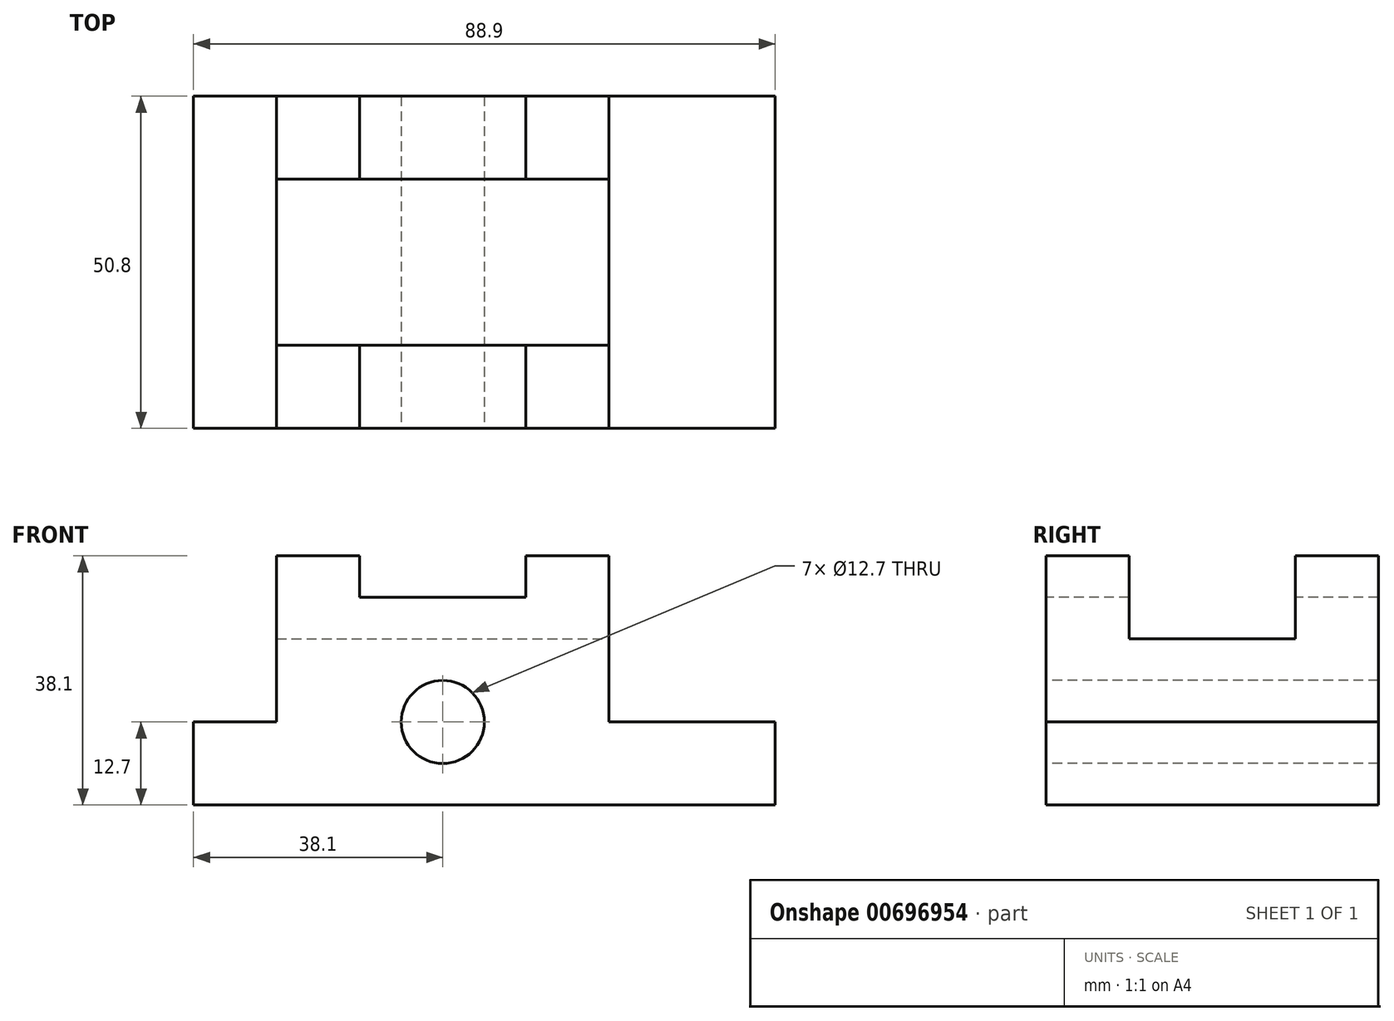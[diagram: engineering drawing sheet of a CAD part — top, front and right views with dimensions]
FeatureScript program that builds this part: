
annotation { "Feature Type Name" : "Feature", "Feature Type Description" : "" }
export const myFeature = defineFeature(function(context is Context, id is Id, definition is map)
    precondition{}
    {
        {
            var Q0;
            Q0=qCreatedBy(makeId("Front.planeOp"),FACE);
            var sketch = newSketch(context, id + "F0", { "sketchPlane" : qUnion([Q0])});
            skLineSegment(sketch, "E0.bottom", {"start": v(-44.45, 19.05) * mm, "end": v(44.45, 19.05) * mm});
            skLineSegment(sketch, "E0.top", {"start": v(-44.45, -19.05) * mm, "end": v(44.45, -19.05) * mm});
            skLineSegment(sketch, "E0.left", {"start": v(-44.45, 19.05) * mm, "end": v(-44.45, -19.05) * mm});
            skLineSegment(sketch, "E0.right", {"start": v(44.45, 19.05) * mm, "end": v(44.45, -19.05) * mm});
            skPoint(sketch, "E0.middle", {"position": v(0, 0) * mm});
            skSolve(sketch);
        }
        {
            var Q0;
            Q0=makeQuery(id+"F0.imprint","IMPRINT",FACE,{"disambiguationData":[TD([[makeQuery(id+"F0.imprint","IMPRINT",EDGE,{"derivedFrom":sQuery(id+"F0.wireOp",EDGE,"E0.bottom")}),-1.0]])]});
            extrude(context, id + "F1", {"entities" : qUnion([Q0]), "depth" : 50.8 * mm, "offsetDistance" : 25.4 * mm});
        }
        {
            var Q0;
            Q0=makeQuery(id+"F1.opExtrude","CAP_FACE",FACE,{"disambiguationData":[OSD([sQuery(id+"F0.wireOp",EDGE,"E0.bottom"),sQuery(id+"F0.wireOp",EDGE,"E0.top"),sQuery(id+"F0.wireOp",EDGE,"E0.left"),sQuery(id+"F0.wireOp",EDGE,"E0.right")])],"isStart":false});
            var sketch = newSketch(context, id + "F2", { "sketchPlane" : qUnion([Q0])});
            skLineSegment(sketch, "E1.bottom", {"start": v(44.45, 19.05) * mm, "end": v(19.05, 19.05) * mm});
            skLineSegment(sketch, "E1.top", {"start": v(44.45, -6.35) * mm, "end": v(19.05, -6.35) * mm});
            skLineSegment(sketch, "E1.left", {"start": v(44.45, 19.05) * mm, "end": v(44.45, -6.35) * mm});
            skLineSegment(sketch, "E1.right", {"start": v(19.05, 19.05) * mm, "end": v(19.05, -6.35) * mm});
            skSolve(sketch);
        }
        {
            var Q0;
            Q0=makeQuery(id+"F2.imprint","IMPRINT",FACE,{"disambiguationData":[TD([[makeQuery(id+"F2.imprint","IMPRINT",EDGE,{"derivedFrom":sQuery(id+"F2.wireOp",EDGE,"E1.bottom")}),-1.0]])]});
            extrude(context, id + "F3", {"entities" : qUnion([Q0]), "operationType" : NewBodyOperationType.REMOVE, "endBound" : BoundingType.THROUGH_ALL, "oppositeDirection" : true, "depth" : 25.4 * mm, "offsetDistance" : 25.4 * mm});
        }
        {
            var Q0;
            Q0=makeQuery(id+"F1.opExtrude","CAP_FACE",FACE,{"disambiguationData":[OSD([sQuery(id+"F0.wireOp",EDGE,"E0.bottom"),sQuery(id+"F0.wireOp",EDGE,"E0.top"),sQuery(id+"F0.wireOp",EDGE,"E0.left"),sQuery(id+"F0.wireOp",EDGE,"E0.right")])],"isStart":false});
            var sketch = newSketch(context, id + "F4", { "sketchPlane" : qUnion([Q0])});
            skLineSegment(sketch, "E2.bottom", {"start": v(-44.45, 19.05) * mm, "end": v(-31.75, 19.05) * mm});
            skLineSegment(sketch, "E2.top", {"start": v(-44.45, -6.35) * mm, "end": v(-31.75, -6.35) * mm});
            skLineSegment(sketch, "E2.left", {"start": v(-44.45, 19.05) * mm, "end": v(-44.45, -6.35) * mm});
            skLineSegment(sketch, "E2.right", {"start": v(-31.75, 19.05) * mm, "end": v(-31.75, -6.35) * mm});
            skSolve(sketch);
        }
        {
            var Q0;
            Q0=makeQuery(id+"F4.imprint","IMPRINT",FACE,{"disambiguationData":[TD([[makeQuery(id+"F4.imprint","IMPRINT",EDGE,{"derivedFrom":sQuery(id+"F4.wireOp",EDGE,"E2.bottom")}),-1.0]])]});
            extrude(context, id + "F5", {"entities" : qUnion([Q0]), "operationType" : NewBodyOperationType.REMOVE, "endBound" : BoundingType.THROUGH_ALL, "oppositeDirection" : true, "depth" : 25.4 * mm, "offsetDistance" : 25.4 * mm});
        }
        {
            var Q0;
            Q0=makeQuery(id+"F1.opExtrude","CAP_FACE",FACE,{"disambiguationData":[OSD([sQuery(id+"F0.wireOp",EDGE,"E0.bottom"),sQuery(id+"F0.wireOp",EDGE,"E0.top"),sQuery(id+"F0.wireOp",EDGE,"E0.left"),sQuery(id+"F0.wireOp",EDGE,"E0.right")])],"isStart":false});
            var sketch = newSketch(context, id + "F6", { "sketchPlane" : qUnion([Q0])});
            skLineSegment(sketch, "E3.bottom", {"start": v(-19.05, 19.05) * mm, "end": v(6.35, 19.05) * mm});
            skLineSegment(sketch, "E3.top", {"start": v(-19.05, 12.7) * mm, "end": v(6.35, 12.7) * mm});
            skLineSegment(sketch, "E3.left", {"start": v(-19.05, 19.05) * mm, "end": v(-19.05, 12.7) * mm});
            skLineSegment(sketch, "E3.right", {"start": v(6.35, 19.05) * mm, "end": v(6.35, 12.7) * mm});
            skSolve(sketch);
        }
        {
            var Q0;
            Q0=makeQuery(id+"F6.imprint","IMPRINT",FACE,{"disambiguationData":[TD([[makeQuery(id+"F6.imprint","IMPRINT",EDGE,{"derivedFrom":sQuery(id+"F6.wireOp",EDGE,"E3.bottom")}),-1.0]])]});
            extrude(context, id + "F7", {"entities" : qUnion([Q0]), "operationType" : NewBodyOperationType.REMOVE, "endBound" : BoundingType.THROUGH_ALL, "oppositeDirection" : true, "depth" : 25.4 * mm, "offsetDistance" : 25.4 * mm});
        }
        {
            var Q0;
            Q0=makeQuery(id+"F3.boolean.opBoolean","COPY",FACE,{"derivedFrom":makeQuery(id+"F3.opExtrude","SWEPT_FACE",FACE,{"disambiguationData":[OSD([sQuery(id+"F2.wireOp",EDGE,"E1.right")])]})});
            var sketch = newSketch(context, id + "F8", { "sketchPlane" : qUnion([Q0])});
            skLineSegment(sketch, "E4.bottom", {"start": v(-38.1, 19.05) * mm, "end": v(-12.7, 19.05) * mm});
            skLineSegment(sketch, "E4.top", {"start": v(-38.1, 6.35) * mm, "end": v(-12.7, 6.35) * mm});
            skLineSegment(sketch, "E4.left", {"start": v(-38.1, 19.05) * mm, "end": v(-38.1, 6.35) * mm});
            skLineSegment(sketch, "E4.right", {"start": v(-12.7, 19.05) * mm, "end": v(-12.7, 6.35) * mm});
            skSolve(sketch);
        }
        {
            var Q0;
            Q0=makeQuery(id+"F8.imprint","IMPRINT",FACE,{"disambiguationData":[TD([[makeQuery(id+"F8.imprint","IMPRINT",EDGE,{"derivedFrom":sQuery(id+"F8.wireOp",EDGE,"E4.bottom")}),1.0]])]});
            extrude(context, id + "F9", {"entities" : qUnion([Q0]), "operationType" : NewBodyOperationType.REMOVE, "endBound" : BoundingType.THROUGH_ALL, "oppositeDirection" : true, "depth" : 25.4 * mm, "offsetDistance" : 25.4 * mm});
        }
        {
            var Q0;
            Q0=makeQuery(id+"F1.opExtrude","CAP_FACE",FACE,{"disambiguationData":[OSD([sQuery(id+"F0.wireOp",EDGE,"E0.bottom"),sQuery(id+"F0.wireOp",EDGE,"E0.top"),sQuery(id+"F0.wireOp",EDGE,"E0.left"),sQuery(id+"F0.wireOp",EDGE,"E0.right")])],"isStart":false});
            var sketch = newSketch(context, id + "F10", { "sketchPlane" : qUnion([Q0])});
            skCircle(sketch, "E5", {"center": v(-6.35, -6.35) * mm, "radius": 6.35 * mm});
            skSolve(sketch);
        }
        {
            var Q0;
            Q0=makeQuery(id+"F10.imprint","IMPRINT",FACE,{"disambiguationData":[TD([[makeQuery(id+"F10.imprint","IMPRINT",EDGE,{"derivedFrom":sQuery(id+"F10.wireOp",EDGE,"E5")}),1.0]])]});
            extrude(context, id + "F11", {"entities" : qUnion([Q0]), "operationType" : NewBodyOperationType.REMOVE, "endBound" : BoundingType.THROUGH_ALL, "oppositeDirection" : true, "depth" : 25.4 * mm, "offsetDistance" : 25.4 * mm});
        }
    });
